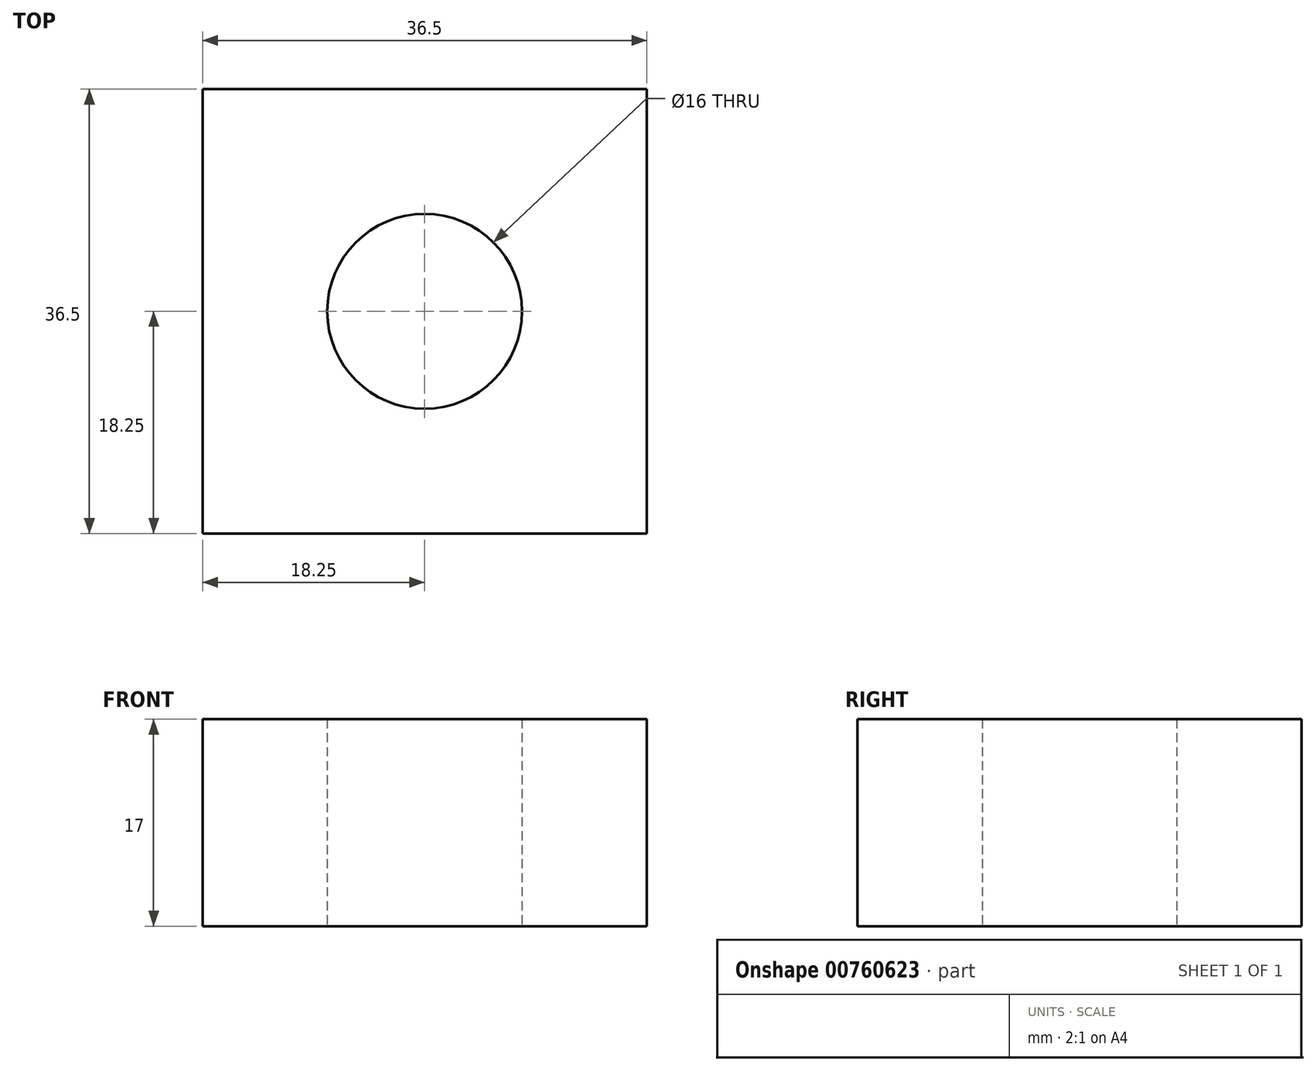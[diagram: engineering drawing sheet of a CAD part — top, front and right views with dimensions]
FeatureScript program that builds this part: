
annotation { "Feature Type Name" : "Feature", "Feature Type Description" : "" }
export const myFeature = defineFeature(function(context is Context, id is Id, definition is map)
    precondition{}
    {
        {
            var Q0;
            Q0=qCreatedBy(makeId("Top.planeOp"),FACE);
            var sketch = newSketch(context, id + "F0", { "sketchPlane" : qUnion([Q0])});
            skCircle(sketch, "E0", {"center": v(0, 0) * mm, "radius": 8 * mm});
            skLineSegment(sketch, "E1.bottom", {"start": v(-18.25, 18.25) * mm, "end": v(18.25, 18.25) * mm});
            skLineSegment(sketch, "E1.top", {"start": v(-18.25, -18.25) * mm, "end": v(18.25, -18.25) * mm});
            skLineSegment(sketch, "E1.left", {"start": v(-18.25, 18.25) * mm, "end": v(-18.25, -18.25) * mm});
            skLineSegment(sketch, "E1.right", {"start": v(18.25, 18.25) * mm, "end": v(18.25, -18.25) * mm});
            skSolve(sketch);
        }
        {
            var Q0;
            Q0 = qSketchRegion(id + "F0", true);
            extrude(context, id + "F1", {"entities" : qUnion([Q0]), "depth" : 17 * mm, "offsetDistance" : 25 * mm});
        }
    });
